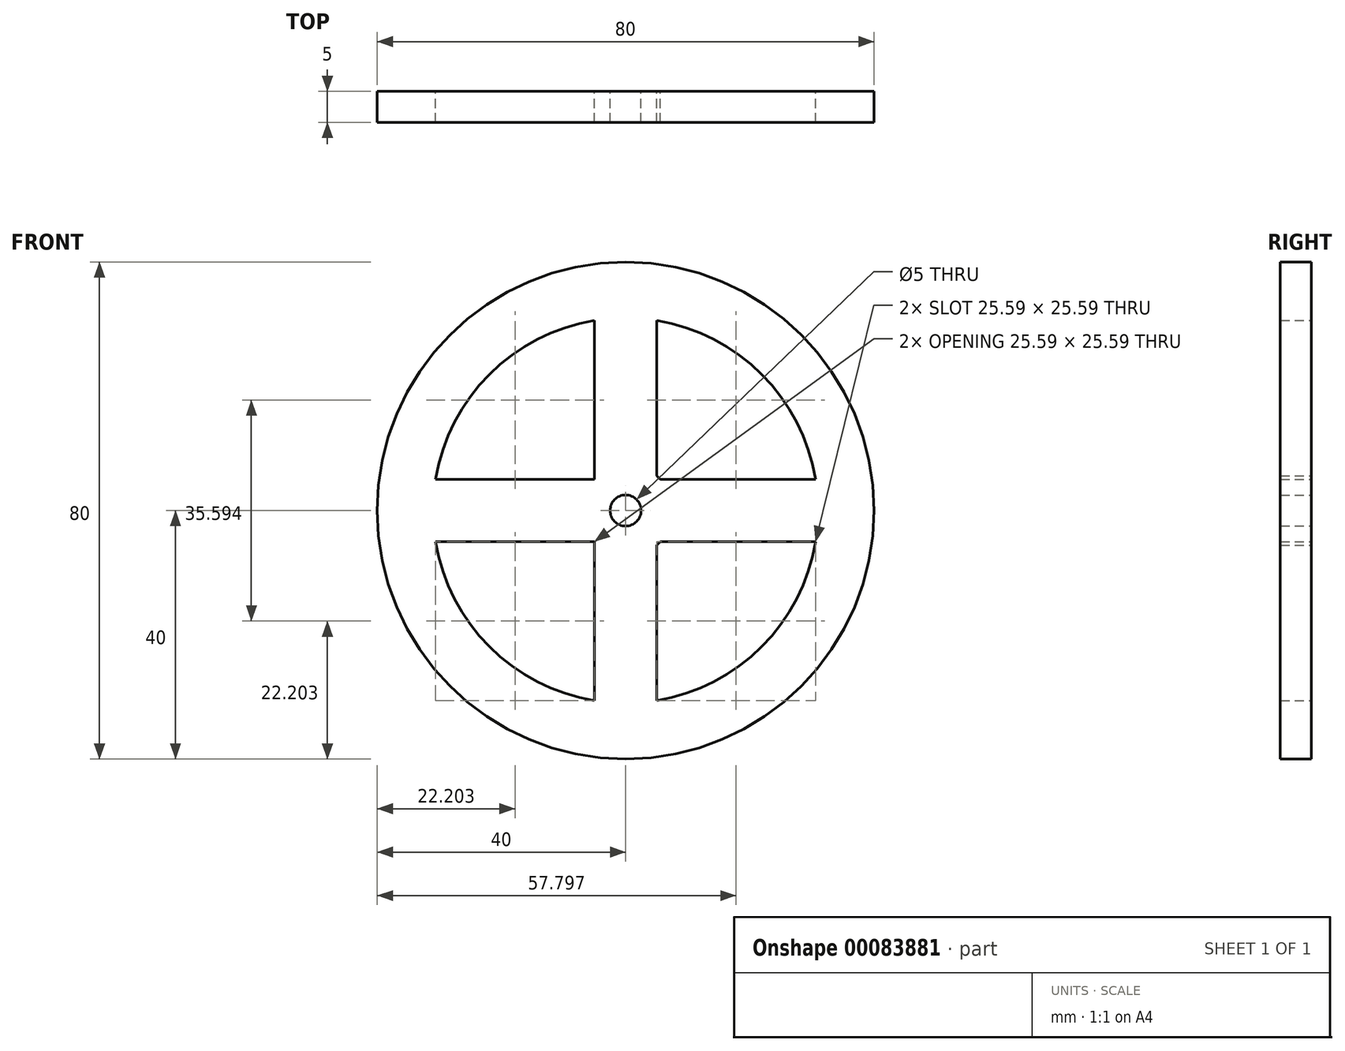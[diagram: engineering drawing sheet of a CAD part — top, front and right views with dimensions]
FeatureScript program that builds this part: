
annotation { "Feature Type Name" : "Feature", "Feature Type Description" : "" }
export const myFeature = defineFeature(function(context is Context, id is Id, definition is map)
    precondition{}
    {
        {
            var Q0;
            Q0=qCreatedBy(makeId("Front.planeOp"),FACE);
            var sketch = newSketch(context, id + "F0", { "sketchPlane" : qUnion([Q0])});
            skCircle(sketch, "E0", {"center": v(0, 0) * mm, "radius": 40 * mm});
            skArc(sketch, "E1", {"start": v(30.6, 5) * mm, "mid": v(21.92, 21.92) * mm, "end": v(5, 30.6) * mm});
            skArc(sketch, "E2", {"start": v(5, -5.6) * mm, "mid": v(5.3, -5.3) * mm, "end": v(5.6, -5) * mm});
            skCircle(sketch, "E3", {"center": v(0, 0) * mm, "radius": 2.5 * mm});
            skLineSegment(sketch, "E4", {"start": v(0, 0) * mm, "end": v(0, 31) * mm, "construction": true});
            skLineSegment(sketch, "E5", {"start": v(0, 0) * mm, "end": v(31, 0) * mm, "construction": true});
            skLineSegment(sketch, "E6", {"start": v(0, 0) * mm, "end": v(0, -31) * mm, "construction": true});
            skLineSegment(sketch, "E7", {"start": v(0, 0) * mm, "end": v(-31, 0) * mm, "construction": true});
            skLineSegment(sketch, "E8.0", {"start": v(5, 5) * mm, "end": v(5, 30.6) * mm});
            skLineSegment(sketch, "E9.0", {"start": v(-5, 5) * mm, "end": v(-5, 30.6) * mm});
            skLineSegment(sketch, "E10.0", {"start": v(5.6, -5) * mm, "end": v(30.6, -5) * mm});
            skLineSegment(sketch, "E11.0", {"start": v(5, -5) * mm, "end": v(5.6, -5) * mm});
            skLineSegment(sketch, "E12.0", {"start": v(-5, -5) * mm, "end": v(-5, -30.6) * mm});
            skLineSegment(sketch, "E13.0", {"start": v(5, -5) * mm, "end": v(30.6, -5) * mm});
            skLineSegment(sketch, "E14.1", {"start": v(-5, -5) * mm, "end": v(-30.6, -5) * mm});
            skLineSegment(sketch, "E15.0", {"start": v(-5.6, -5) * mm, "end": v(-30.6, -5) * mm});
            skLineSegment(sketch, "E16.0", {"start": v(-5, 5) * mm, "end": v(-30.6, 5) * mm});
            skLineSegment(sketch, "E17.0", {"start": v(5.6, 5) * mm, "end": v(30.6, 5) * mm});
            skLineSegment(sketch, "E18.0", {"start": v(5, -5.6) * mm, "end": v(5, -30.6) * mm});
            skLineSegment(sketch, "E19.trimOffspring", {"start": v(5, 39.69) * mm, "end": v(5, 40) * mm});
            skLineSegment(sketch, "E20.trimOffspring", {"start": v(-5, 39.69) * mm, "end": v(-5, 40) * mm});
            skLineSegment(sketch, "E21.trimOffspring", {"start": v(39.69, 5) * mm, "end": v(40, 5) * mm});
            skLineSegment(sketch, "E22.trimOffspring", {"start": v(39.69, -5) * mm, "end": v(40, -5) * mm});
            skLineSegment(sketch, "E23.trimOffspring", {"start": v(5, -39.69) * mm, "end": v(5, -40) * mm});
            skLineSegment(sketch, "E24.trimOffspring", {"start": v(-39.69, -5) * mm, "end": v(-40, -5) * mm});
            skLineSegment(sketch, "E25.trimOffspring", {"start": v(-39.69, 5) * mm, "end": v(-40, 5) * mm});
            skArc(sketch, "E26.trimOffspring", {"start": v(-30.6, -5) * mm, "mid": v(-21.92, -21.92) * mm, "end": v(-5, -30.6) * mm});
            skLineSegment(sketch, "E27.trimOffspring", {"start": v(-5, -39.69) * mm, "end": v(-5, -40) * mm});
            skArc(sketch, "E28.trimOffspring", {"start": v(5, -30.6) * mm, "mid": v(21.92, -21.92) * mm, "end": v(30.6, -5) * mm});
            skArc(sketch, "E29.trimOffspring", {"start": v(-5, 30.6) * mm, "mid": v(-21.92, 21.92) * mm, "end": v(-30.6, 5) * mm});
            skArc(sketch, "E30.trimOffspring", {"start": v(5.6, 5) * mm, "mid": v(5.3, 5.3) * mm, "end": v(5, 5.6) * mm});
            skLineSegment(sketch, "E31.trimOffspring", {"start": v(-5.6, -5) * mm, "end": v(-5.6, -5) * mm});
            skSolve(sketch);
        }
        {
            var Q0;
            {var subQ4=sQuery(id+"F0.wireOp",EDGE,"E1");Q0=makeQuery(id+"F0.imprint","IMPRINT",FACE,{"disambiguationData":[TD([[makeQuery(id+"F0.imprint","IMPRINT",EDGE,{"derivedFrom":subQ4}),-1.0]])]});}
            extrude(context, id + "F1", {"entities" : qUnion([Q0]), "endBound" : BoundingType.SYMMETRIC, "depth" : 5 * mm});
        }
    });
